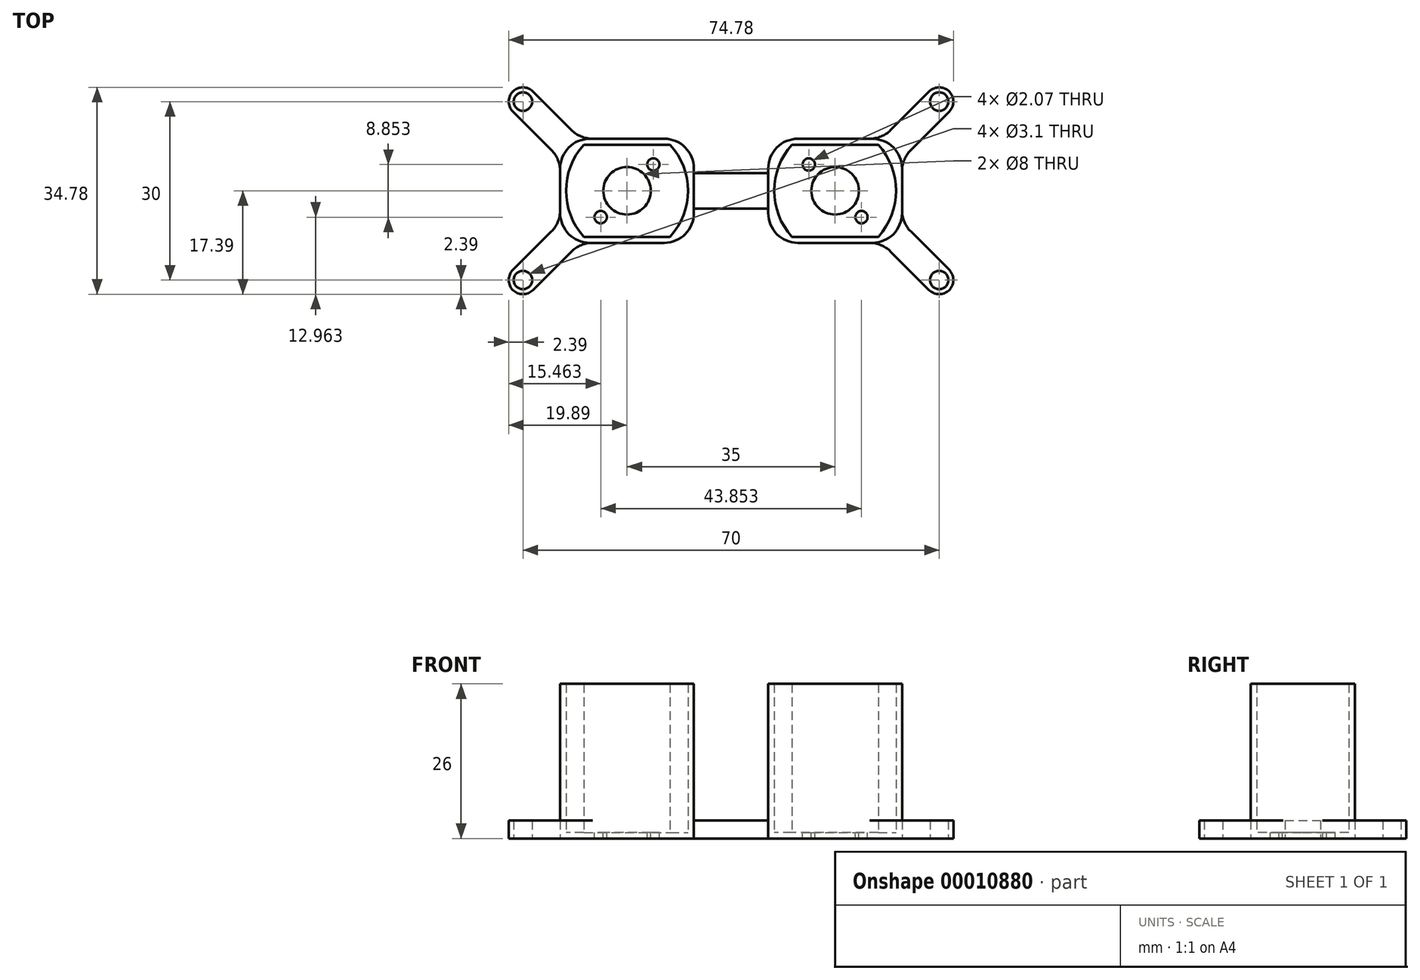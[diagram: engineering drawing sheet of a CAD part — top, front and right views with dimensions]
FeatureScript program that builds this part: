
annotation { "Feature Type Name" : "Feature", "Feature Type Description" : "" }
export const myFeature = defineFeature(function(context is Context, id is Id, definition is map)
    precondition{}
    {
        {
            var Q0;
            Q0=qCreatedBy(makeId("Top.planeOp"),FACE);
            var sketch = newSketch(context, id + "F0", { "sketchPlane" : qUnion([Q0])});
            skLineSegment(sketch, "E0.bottom", {"start": v(-7.25, 7.75) * mm, "end": v(7.25, 7.75) * mm});
            skLineSegment(sketch, "E0.top", {"start": v(-7.25, -7.75) * mm, "end": v(7.25, -7.75) * mm});
            skLineSegment(sketch, "E0.left", {"start": v(-7.25, 7.75) * mm, "end": v(-7.25, -7.75) * mm, "construction": true});
            skLineSegment(sketch, "E0.right", {"start": v(7.25, 7.75) * mm, "end": v(7.25, -7.75) * mm, "construction": true});
            skArc(sketch, "E1", {"start": v(-7.25, 7.75) * mm, "mid": v(-10.25, 0) * mm, "end": v(-7.25, -7.75) * mm});
            skArc(sketch, "E2", {"start": v(7.25, -7.75) * mm, "mid": v(10.25, 0) * mm, "end": v(7.25, 7.75) * mm});
            skLineSegment(sketch, "E3", {"start": v(-7.25, 7.75) * mm, "end": v(-10.25, 7.75) * mm, "construction": true});
            skLineSegment(sketch, "E4", {"start": v(-10.25, 7.75) * mm, "end": v(-10.25, -7.75) * mm, "construction": true});
            skLineSegment(sketch, "E5", {"start": v(-10.25, -7.75) * mm, "end": v(-7.25, -7.75) * mm, "construction": true});
            skLineSegment(sketch, "E6", {"start": v(7.25, -7.75) * mm, "end": v(10.25, -7.75) * mm, "construction": true});
            skLineSegment(sketch, "E7", {"start": v(10.25, -7.75) * mm, "end": v(10.25, 7.75) * mm, "construction": true});
            skLineSegment(sketch, "E8", {"start": v(10.25, 7.75) * mm, "end": v(7.25, 7.75) * mm, "construction": true});
            skLineSegment(sketch, "E9.bottom", {"start": v(-11.25, 8.75) * mm, "end": v(11.25, 8.75) * mm});
            skLineSegment(sketch, "E9.top", {"start": v(-11.25, -8.75) * mm, "end": v(11.25, -8.75) * mm});
            skLineSegment(sketch, "E9.left", {"start": v(-11.25, 8.75) * mm, "end": v(-11.25, -8.75) * mm});
            skLineSegment(sketch, "E9.right", {"start": v(11.25, 8.75) * mm, "end": v(11.25, -8.75) * mm});
            skPoint(sketch, "E10.visualSharp", {"position": v(-11.25, 8.75) * mm});
            skPoint(sketch, "E11.visualSharp", {"position": v(11.25, 8.75) * mm});
            skPoint(sketch, "E12.visualSharp", {"position": v(11.25, -8.75) * mm});
            skPoint(sketch, "E13.visualSharp", {"position": v(-11.25, -8.75) * mm});
            skLineSegment(sketch, "E14", {"start": v(-1.26, 0) * mm, "end": v(1.26, 0) * mm, "construction": true});
            skPoint(sketch, "E15", {"position": v(0, 0) * mm});
            skLineSegment(sketch, "E16", {"start": v(10.25, -7.75) * mm, "end": v(10.25, -8.75) * mm, "construction": true});
            skLineSegment(sketch, "E17", {"start": v(-10.25, 7.75) * mm, "end": v(-10.25, 8.75) * mm, "construction": true});
            skLineSegment(sketch, "E18", {"start": v(-10.25, 7.75) * mm, "end": v(-11.25, 7.75) * mm, "construction": true});
            skLineSegment(sketch, "E19", {"start": v(10.25, -7.75) * mm, "end": v(11.25, -7.75) * mm, "construction": true});
            skSolve(sketch);
        }
        {
            var Q0;
            Q0=qSketchRegion(id+"F0",true);
            extrude(context, id + "F1", {"entities" : qUnion([Q0]), "depth" : 25 * mm});
        }
        {
            var Q0;
            Q0=qCreatedBy(makeId("Top.planeOp"),FACE);
            var sketch = newSketch(context, id + "F2", { "sketchPlane" : qUnion([Q0])});
            skCircle(sketch, "E20", {"center": v(0, 0) * mm, "radius": 4 * mm});
            skLineSegment(sketch, "E21", {"start": v(-4.43, -4.43) * mm, "end": v(4.43, 4.43) * mm, "construction": true});
            skCircle(sketch, "E22", {"center": v(-4.43, -4.43) * mm, "radius": 1.04 * mm});
            skCircle(sketch, "E23", {"center": v(4.43, 4.43) * mm, "radius": 1.04 * mm});
            skLineSegment(sketch, "E24", {"start": v(0, 0) * mm, "end": v(0, -4) * mm, "construction": true});
            skLineSegment(sketch, "E25.bottom", {"start": v(-11.25, -8.75) * mm, "end": v(11.25, -8.75) * mm});
            skLineSegment(sketch, "E25.top", {"start": v(-11.25, 8.75) * mm, "end": v(11.25, 8.75) * mm});
            skLineSegment(sketch, "E25.left", {"start": v(-11.25, -8.75) * mm, "end": v(-11.25, 8.75) * mm});
            skLineSegment(sketch, "E25.right", {"start": v(11.25, -8.75) * mm, "end": v(11.25, 8.75) * mm});
            skSolve(sketch);
        }
        {
            var Q0;
            Q0=qSketchRegion(id+"F2",true);
            extrude(context, id + "F3", {"entities" : qUnion([Q0]), "operationType" : NewBodyOperationType.ADD, "oppositeDirection" : true, "depth" : 1 * mm});
        }
        {
            var Q0;
            Q0=makeQuery(id+"F3.opExtrude","CAP_FACE",FACE,{"disambiguationData":[OSD([sQuery(id+"F2.wireOp",EDGE,"9aef3d48-fcec-49af-8fe0-c07a83de9d9d.bottom"),sQuery(id+"F2.wireOp",EDGE,"9aef3d48-fcec-49af-8fe0-c07a83de9d9d.top"),sQuery(id+"F2.wireOp",EDGE,"9aef3d48-fcec-49af-8fe0-c07a83de9d9d.left"),sQuery(id+"F2.wireOp",EDGE,"9aef3d48-fcec-49af-8fe0-c07a83de9d9d.right"),sQuery(id+"F2.wireOp",EDGE,"60c8d90f-e83d-42f8-a0dd-aa9fc3caf3ca.filletArc"),sQuery(id+"F2.wireOp",EDGE,"e39097f1-45af-4b58-a32d-9713a406a2f0.filletArc"),sQuery(id+"F2.wireOp",EDGE,"80603ea1-f281-4a3c-b745-80a3f8f7ce23.filletArc"),sQuery(id+"F2.wireOp",EDGE,"1a4f9cfa-e126-41bd-9235-e0dfa8cf3aca.filletArc"),sQuery(id+"F2.wireOp",EDGE,"E20"),sQuery(id+"F2.wireOp",EDGE,"E22"),sQuery(id+"F2.wireOp",EDGE,"E23")])],"isStart":false});
            var sketch = newSketch(context, id + "F4", { "sketchPlane" : qUnion([Q0])});
            skCircle(sketch, "E26", {"center": v(0, 0) * mm, "radius": 17.67 * mm, "construction": true});
            skLineSegment(sketch, "E27", {"start": v(-9.34, 10.21) * mm, "end": v(-15.81, 16.69) * mm});
            skLineSegment(sketch, "E28", {"start": v(-12.71, 6.84) * mm, "end": v(-19.19, 13.31) * mm});
            skLineSegment(sketch, "E29", {"start": v(-11.25, 8.75) * mm, "end": v(-17.5, 15) * mm, "construction": true});
            skArc(sketch, "E30", {"start": v(-15.81, 16.69) * mm, "mid": v(-19.19, 16.69) * mm, "end": v(-19.19, 13.31) * mm});
            skLineSegment(sketch, "E31", {"start": v(-19.19, 13.31) * mm, "end": v(-15.81, 16.69) * mm, "construction": true});
            skCircle(sketch, "E32", {"center": v(-17.5, 15) * mm, "radius": 1.55 * mm});
            skLineSegment(sketch, "E33", {"start": v(-7.87, 8.75) * mm, "end": v(-11.25, 8.75) * mm, "construction": true});
            skLineSegment(sketch, "E34", {"start": v(-11.25, 8.75) * mm, "end": v(-11.25, 5.37) * mm, "construction": true});
            skPoint(sketch, "E35.visualSharp", {"position": v(-7.87, 8.75) * mm});
            skArc(sketch, "E35.filletArc", {"start": v(-9.34, 10.21) * mm, "mid": v(-7.71, 9.13) * mm, "end": v(-5.8, 8.75) * mm});
            skPoint(sketch, "E36.visualSharp", {"position": v(-11.25, 5.37) * mm});
            skArc(sketch, "E36.filletArc", {"start": v(-11.25, 3.3) * mm, "mid": v(-11.63, 5.21) * mm, "end": v(-12.71, 6.84) * mm});
            skLineSegment(sketch, "E37", {"start": v(-11.25, 3.3) * mm, "end": v(-11.25, 8.75) * mm});
            skLineSegment(sketch, "E38", {"start": v(-5.8, 8.75) * mm, "end": v(-11.25, 8.75) * mm});
            skSolve(sketch);
        }
        {
            var Q0;
            Q0=qSketchRegion(id+"F4",true);
            extrude(context, id + "F5", {"entities" : qUnion([Q0]), "oppositeDirection" : true, "depth" : 3 * mm});
        }
        {
            var Q0;
            Q0=makeQuery(id+"F5.opExtrude","SWEPT_BODY",BODY,{"disambiguationData":[OSD([sQuery(id+"F4.wireOp",EDGE,"E27"),sQuery(id+"F4.wireOp",EDGE,"E28"),sQuery(id+"F4.wireOp",EDGE,"E30"),sQuery(id+"F4.wireOp",EDGE,"E32"),sQuery(id+"F4.wireOp",EDGE,"E35.filletArc"),sQuery(id+"F4.wireOp",EDGE,"E36.filletArc"),sQuery(id+"F4.wireOp",EDGE,"E37"),sQuery(id+"F4.wireOp",EDGE,"E38")])]});
            var Q1;
            Q1=qCreatedBy(makeId("Front.planeOp"),FACE);
            mirror(context, id + "F6", {"operationType" : NewBodyOperationType.ADD, "entities" : qUnion([Q0]), "mirrorPlane" : qUnion([Q1])});
        }
        {
            var Q0;
            Q0=makeQuery(id+"F3.boolean.opBoolean","MERGE",EDGE,{"derivedFrom":[makeQuery(id+"F1.opExtrude","SWEPT_EDGE",EDGE,{"disambiguationData":[OSD([sQuery(id+"F0.wireOp",EDGE,"E9.bottom"),sQuery(id+"F0.wireOp",EDGE,"E9.left")])]}),makeQuery(id+"F3.opExtrude","SWEPT_EDGE",EDGE,{"disambiguationData":[OSD([sQuery(id+"F2.wireOp",EDGE,"E25.top"),sQuery(id+"F2.wireOp",EDGE,"E25.left")])]})]});
            var Q1;
            Q1=makeQuery(id+"F3.boolean.opBoolean","MERGE",EDGE,{"derivedFrom":[makeQuery(id+"F1.opExtrude","SWEPT_EDGE",EDGE,{"disambiguationData":[OSD([sQuery(id+"F0.wireOp",EDGE,"E9.top"),sQuery(id+"F0.wireOp",EDGE,"E9.left")])]}),makeQuery(id+"F3.opExtrude","SWEPT_EDGE",EDGE,{"disambiguationData":[OSD([sQuery(id+"F2.wireOp",EDGE,"E25.bottom"),sQuery(id+"F2.wireOp",EDGE,"E25.left")])]})]});
            var Q2;
            Q2=makeQuery(id+"F3.boolean.opBoolean","MERGE",EDGE,{"derivedFrom":[makeQuery(id+"F1.opExtrude","SWEPT_EDGE",EDGE,{"disambiguationData":[OSD([sQuery(id+"F0.wireOp",EDGE,"E9.top"),sQuery(id+"F0.wireOp",EDGE,"E9.right")])]}),makeQuery(id+"F3.opExtrude","SWEPT_EDGE",EDGE,{"disambiguationData":[OSD([sQuery(id+"F2.wireOp",EDGE,"E25.bottom"),sQuery(id+"F2.wireOp",EDGE,"E25.right")])]})]});
            var Q3;
            Q3=makeQuery(id+"F3.boolean.opBoolean","MERGE",EDGE,{"derivedFrom":[makeQuery(id+"F1.opExtrude","SWEPT_EDGE",EDGE,{"disambiguationData":[OSD([sQuery(id+"F0.wireOp",EDGE,"E9.bottom"),sQuery(id+"F0.wireOp",EDGE,"E9.right")])]}),makeQuery(id+"F3.opExtrude","SWEPT_EDGE",EDGE,{"disambiguationData":[OSD([sQuery(id+"F2.wireOp",EDGE,"E25.top"),sQuery(id+"F2.wireOp",EDGE,"E25.right")])]})]});
            fillet(context, id + "F7", {"entities" : qUnion([Q0, Q1, Q2, Q3]), "radius" : 5 * mm, "tangentPropagation" : true, "allowEdgeOverflow" : false});
        }
        {
            var Q0;
            {var subQ0=makeQuery(id+"F5.opExtrude","CAP_FACE",FACE,{"disambiguationData":[OSD([sQuery(id+"F4.wireOp",EDGE,"E27"),sQuery(id+"F4.wireOp",EDGE,"E28"),sQuery(id+"F4.wireOp",EDGE,"E30"),sQuery(id+"F4.wireOp",EDGE,"E32"),sQuery(id+"F4.wireOp",EDGE,"E35.filletArc"),sQuery(id+"F4.wireOp",EDGE,"E36.filletArc"),sQuery(id+"F4.wireOp",EDGE,"E37"),sQuery(id+"F4.wireOp",EDGE,"E38")])],"isStart":true});Q0=makeQuery(id+"F6.boolean.opBoolean","MERGE",FACE,{"derivedFrom":[makeQuery(id+"F3.opExtrude","CAP_FACE",FACE,{"disambiguationData":[OSD([sQuery(id+"F2.wireOp",EDGE,"E20"),sQuery(id+"F2.wireOp",EDGE,"E22"),sQuery(id+"F2.wireOp",EDGE,"E23"),sQuery(id+"F2.wireOp",EDGE,"E25.bottom"),sQuery(id+"F2.wireOp",EDGE,"E25.top"),sQuery(id+"F2.wireOp",EDGE,"E25.left"),sQuery(id+"F2.wireOp",EDGE,"E25.right")])],"isStart":false}),subQ0,makeQuery(id+"F6.opPattern","COPY",FACE,{"derivedFrom":subQ0,"instanceName":"1"})]});}
            var sketch = newSketch(context, id + "F8", { "sketchPlane" : qUnion([Q0])});
            skLineSegment(sketch, "E39.bottom", {"start": v(11.25, 3) * mm, "end": v(17.5, 3) * mm});
            skLineSegment(sketch, "E39.top", {"start": v(11.25, -3) * mm, "end": v(17.5, -3) * mm});
            skLineSegment(sketch, "E39.left", {"start": v(11.25, 3) * mm, "end": v(11.25, -3) * mm});
            skLineSegment(sketch, "E39.right", {"start": v(17.5, 3) * mm, "end": v(17.5, -3) * mm});
            skPoint(sketch, "E40", {"position": v(11.25, 0) * mm});
            skSolve(sketch);
        }
        {
            var Q0;
            Q0 = qSketchRegion(id + "F8", true);
            extrude(context, id + "F9", {"entities" : qUnion([Q0]), "operationType" : NewBodyOperationType.ADD, "oppositeDirection" : true, "depth" : 3 * mm});
        }
        {
            var Q0;
            Q0=makeQuery(id+"F1.opExtrude","SWEPT_BODY",BODY,{"disambiguationData":[OSD([sQuery(id+"F0.wireOp",EDGE,"E0.bottom"),sQuery(id+"F0.wireOp",EDGE,"E0.top"),sQuery(id+"F0.wireOp",EDGE,"E1"),sQuery(id+"F0.wireOp",EDGE,"E2"),sQuery(id+"F0.wireOp",EDGE,"E9.bottom"),sQuery(id+"F0.wireOp",EDGE,"E9.top"),sQuery(id+"F0.wireOp",EDGE,"E9.left"),sQuery(id+"F0.wireOp",EDGE,"E9.right")])]});
            var Q1;
            Q1=makeQuery(id+"F9.opExtrude","SWEPT_FACE",FACE,{"disambiguationData":[OSD([sQuery(id+"F8.wireOp",EDGE,"E39.right")])]});
            mirror(context, id + "F10", {"operationType" : NewBodyOperationType.ADD, "entities" : qUnion([Q0]), "mirrorPlane" : qUnion([Q1])});
        }
    });
